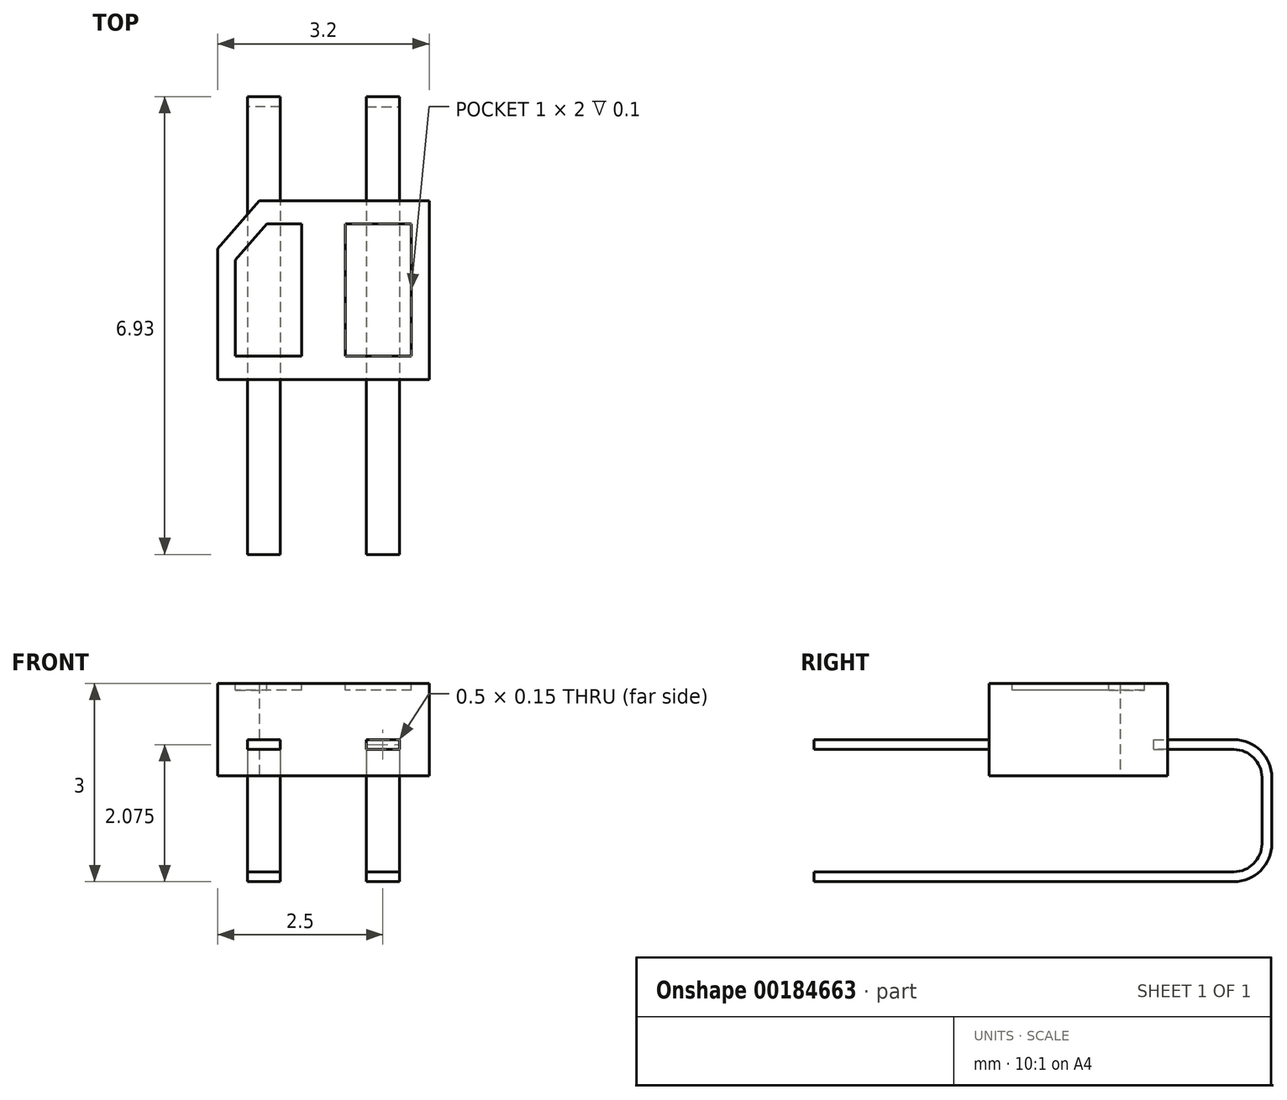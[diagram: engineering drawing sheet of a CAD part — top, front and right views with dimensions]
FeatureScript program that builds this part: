
annotation { "Feature Type Name" : "Feature", "Feature Type Description" : "" }
export const myFeature = defineFeature(function(context is Context, id is Id, definition is map)
    precondition{}
    {
        {
            var Q0;
            Q0=qCreatedBy(makeId("Top.planeOp"),FACE);
            var sketch = newSketch(context, id + "F0", { "sketchPlane" : qUnion([Q0])});
            skLineSegment(sketch, "E0.bottom", {"start": v(1.6, 1.35) * mm, "end": v(-0.97, 1.35) * mm});
            skLineSegment(sketch, "E0.top", {"start": v(1.6, -1.35) * mm, "end": v(-1.6, -1.35) * mm});
            skLineSegment(sketch, "E0.left", {"start": v(1.6, 1.35) * mm, "end": v(1.6, -1.35) * mm});
            skLineSegment(sketch, "E0.right", {"start": v(-1.6, 0.63) * mm, "end": v(-1.6, -1.35) * mm});
            skPoint(sketch, "E0.middle", {"position": v(0, 0) * mm});
            skLineSegment(sketch, "E1", {"start": v(-1.6, 0.63) * mm, "end": v(-0.97, 1.35) * mm});
            skPoint(sketch, "E2.orphan", {"position": v(-1.6, 1.35) * mm});
            skSolve(sketch);
        }
        {
            var Q0;
            Q0=qSketchRegion(id+"F0",true);
            extrude(context, id + "F1", {"entities" : qUnion([Q0]), "depth" : 1.4 * mm});
        }
        {
            var Q0;
            Q0=makeQuery(id+"F1.opExtrude","CAP_FACE",FACE,{"disambiguationData":[OSD([sQuery(id+"F0.wireOp",EDGE,"E0.bottom"),sQuery(id+"F0.wireOp",EDGE,"E0.top"),sQuery(id+"F0.wireOp",EDGE,"E0.left"),sQuery(id+"F0.wireOp",EDGE,"E0.right"),sQuery(id+"F0.wireOp",EDGE,"E1")])],"isStart":false});
            var sketch = newSketch(context, id + "F2", { "sketchPlane" : qUnion([Q0])});
            skLineSegment(sketch, "E3.bottom", {"start": v(1.33, 1) * mm, "end": v(0.33, 1) * mm});
            skLineSegment(sketch, "E3.top", {"start": v(1.33, -1) * mm, "end": v(0.33, -1) * mm});
            skLineSegment(sketch, "E3.left", {"start": v(1.33, 1) * mm, "end": v(1.33, -1) * mm});
            skLineSegment(sketch, "E3.right", {"start": v(0.33, 1) * mm, "end": v(0.33, -1) * mm});
            skPoint(sketch, "E3.middle", {"position": v(0.83, 0) * mm});
            skLineSegment(sketch, "E4.bottom", {"start": v(-0.33, 1) * mm, "end": v(-0.85, 1) * mm});
            skLineSegment(sketch, "E4.top", {"start": v(-0.33, -1) * mm, "end": v(-1.33, -1) * mm});
            skLineSegment(sketch, "E4.left", {"start": v(-0.33, 1) * mm, "end": v(-0.33, -1) * mm});
            skLineSegment(sketch, "E4.right", {"start": v(-1.33, 0.46) * mm, "end": v(-1.33, -1) * mm});
            skPoint(sketch, "E4.middle", {"position": v(-0.83, 0) * mm});
            skLineSegment(sketch, "E5", {"start": v(-1.33, 0.46) * mm, "end": v(-0.85, 1) * mm});
            skPoint(sketch, "E6.orphan", {"position": v(-1.33, 1) * mm});
            skSolve(sketch);
        }
        {
            var Q0;
            Q0=qSketchRegion(id+"F2",true);
            extrude(context, id + "F3", {"entities" : qUnion([Q0]), "operationType" : NewBodyOperationType.REMOVE, "oppositeDirection" : true, "depth" : 0.1 * mm});
        }
        {
            var Q0;
            Q0=qCreatedBy(makeId("Front.planeOp"),FACE);
            var sketch = newSketch(context, id + "F4", { "sketchPlane" : qUnion([Q0])});
            skLineSegment(sketch, "E7.bottom", {"start": v(-0.65, 0.4) * mm, "end": v(-1.15, 0.4) * mm});
            skLineSegment(sketch, "E7.top", {"start": v(-0.65, 0.55) * mm, "end": v(-1.15, 0.55) * mm});
            skLineSegment(sketch, "E7.left", {"start": v(-0.65, 0.4) * mm, "end": v(-0.65, 0.55) * mm});
            skLineSegment(sketch, "E7.right", {"start": v(-1.15, 0.4) * mm, "end": v(-1.15, 0.55) * mm});
            skPoint(sketch, "E7.middle", {"position": v(-0.9, 0.47) * mm});
            skSolve(sketch);
        }
        {
            var Q0;
            Q0=qSketchRegion(id+"F4",true);
            extrude(context, id + "F5", {"entities" : qUnion([Q0]), "depth" : 4 * mm});
        }
        {
            var Q0;
            Q0=makeQuery(id+"F5.opExtrude","SWEPT_BODY",BODY,{"disambiguationData":[OSD([sQuery(id+"F4.wireOp",EDGE,"E7.bottom"),sQuery(id+"F4.wireOp",EDGE,"E7.top"),sQuery(id+"F4.wireOp",EDGE,"E7.left"),sQuery(id+"F4.wireOp",EDGE,"E7.right")])]});
            var Q1;
            Q1=qCreatedBy(makeId("Right.planeOp"),FACE);
            mirror(context, id + "F6", {"operationType" : NewBodyOperationType.ADD, "entities" : qUnion([Q0]), "mirrorPlane" : qUnion([Q1])});
        }
        {
            var Q0;
            Q0=qCreatedBy(makeId("Right.planeOp"),FACE);
            cPlane(context, id + "F7", {"entities" : qUnion([Q0]), "cplaneType" : CPlaneType.OFFSET, "offset" : 0.9 * mm, "oppositeDirection" : true, "width" : 150 * mm, "height" : 150 * mm});
        }
        {
            var Q0;
            Q0=qCreatedBy(id+"F7.planeOp",FACE);
            var sketch = newSketch(context, id + "F8", { "sketchPlane" : qUnion([Q0])});
            skLineSegment(sketch, "E8", {"start": v(0, 0.47) * mm, "end": v(2.35, 0.47) * mm});
            skLineSegment(sketch, "E9", {"start": v(2.85, -0.03) * mm, "end": v(2.85, -1.02) * mm});
            skLineSegment(sketch, "E10", {"start": v(2.35, -1.52) * mm, "end": v(-4, -1.52) * mm});
            skPoint(sketch, "E11.visualSharp", {"position": v(2.85, 0.47) * mm});
            skArc(sketch, "E11.filletArc", {"start": v(2.85, -0.03) * mm, "mid": v(2.7, 0.33) * mm, "end": v(2.35, 0.47) * mm});
            skPoint(sketch, "E12.visualSharp", {"position": v(2.85, -1.52) * mm});
            skArc(sketch, "E12.filletArc", {"start": v(2.35, -1.52) * mm, "mid": v(2.7, -1.38) * mm, "end": v(2.85, -1.02) * mm});
            skLineSegment(sketch, "E13.0", {"start": v(-4, 0.4) * mm, "end": v(-4, 0.55) * mm, "construction": true});
            skPoint(sketch, "E14", {"position": v(-4, 0.47) * mm});
            skSolve(sketch);
        }
        {
            var Q0;
            Q0=makeQuery(id+"F4.imprint","IMPRINT",FACE,{"disambiguationData":[TD([[makeQuery(id+"F4.imprint","IMPRINT",EDGE,{"derivedFrom":sQuery(id+"F4.wireOp",EDGE,"E7.bottom")}),-1.0]])]});
            var Q1;
            Q1=qConstructionFilter(qBodyType(qCreatedBy(id+"F8",EDGE),BodyType.WIRE),ConstructionObject.NO);
            sweep(context, id + "F9", {"profiles" : qUnion([Q0]), "path" : qUnion([Q1])});
        }
        {
            var Q0;
            Q0=makeQuery(id+"F9.opSweep","SWEPT_BODY",BODY,{"disambiguationData":[OSD([sQuery(id+"F4.wireOp",EDGE,"E7.bottom"),sQuery(id+"F4.wireOp",EDGE,"E7.top"),sQuery(id+"F4.wireOp",EDGE,"E7.left"),sQuery(id+"F4.wireOp",EDGE,"E7.right"),sQuery(id+"F8.wireOp",EDGE,"E8")])]});
            var Q1;
            Q1=qCreatedBy(makeId("Right.planeOp"),FACE);
            mirror(context, id + "F10", {"operationType" : NewBodyOperationType.ADD, "entities" : qUnion([Q0]), "mirrorPlane" : qUnion([Q1])});
        }
    });
